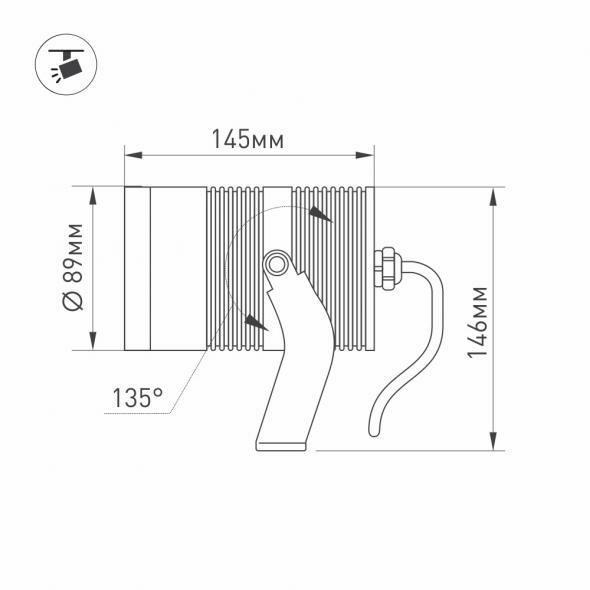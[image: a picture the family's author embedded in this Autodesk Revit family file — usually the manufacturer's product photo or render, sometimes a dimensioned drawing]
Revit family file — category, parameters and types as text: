
# Revit family: RAY-R89
name_source: partatom
category: Осветительные приборы
revit_build: Autodesk Revit 2017 (Build: 20160225_1515(x64)
units: mm (PartAtom-declared; Revit-internal decimal feet)

## family parameters
Всегда вертикально = Да
Источник света = Да
На основе рабочей плоскости = Нет
Общий = Нет
При загрузке вырезать с полостями = Нет
Размер круглого соединителя = Использовать диаметр
Тип детали = Нормальный
Точка расчета площади = Нет

## types (3) — shared parameters
ADSK_Единица измерения = шт.
ADSK_Завод-изготовитель = ARLIGHT
ADSK_Классификация нагрузок = Освещение
ADSK_Количество фаз = 1
ADSK_Количество фаз числовое = 1
ADSK_Коэффициент мощности = 0.96
ADSK_Масса_Текст = 1.37
ADSK_Наименование = Светильник
ADSK_Напряжение = 230 В
ADSK_Номинальная мощность = 25 Вт
ADSK_Полная мощность = 26 В·А
ADSK_Размер_Высота = 146 мм
ADSK_Размер_Диаметр = 89 мм
ADSK_Размер_Длина = 145 мм
ADSK_Ток = 0 А
ARL_Драйвер = Встроенный
ARL_Индекс цветопередачи = >80
ARL_Класс защиты от поражения электрическим током = I
ARL_Класс пылевлагозащиты = IP67
ARL_Материал корпуса = Металл, темно-серый
ARL_Область использования = Для ландшафтного освещения парковых и садовых дорожек, придомовых территорий, а также декоративной подсветки фасадов
ARL_Обозначение корпуса = Корпус круглый, алюминий, цвет темно-серый
ARL_Серия = RAY
ARL_Способ монтажа = Кронштейн
ARL_Тип товара = Светильник
ARL_Угол обзора = 24°
ARL_Цвет покрытия = Темно-серый
URL = https://arlight.ru
Видимая форма излучения при визуализации = Нет
Группа модели = Светильники
Изготовитель = ARLIGHT
Изготовитель (сайт) = www.arlight.ru
Изготовитель (телефон) = 8 800 505 26 29
Излучение по диаметру окружности = 67.55 мм
Полная установленная мощность = 26 В·А
Разработчик = НТЦ Конструктор
Разработчик (URL) = https://constructor.ru
Разработчик (телефон) = +7 (495) 781-05-35
Светофильтр = 16777215
Смещение цветовой температуры при затухании лампы = <Нет>
Угол наклона = 90.00°

## per-type parameters (varying)
| type | ADSK_Код изделия | ADSK_Марка | ARL_Рабочая температура окружающей среды | ARL_Цвет свечения | Комментарии к типоразмеру | Описание | Файл фотометрической сетки |
| 029699 Светильник ALT-RAY-R89-25W Day4000 (DG, 24 deg, 230V) | Арт. 029699 | ALT-RAY-R89-25W Day4000 | -40...+60 °C | Дневной 4000K | Арт. 029699 | Уличный светодиодный светильник, мощность 25 Вт, угол освещения 24°. Цвет ДНЕВНОЙ 4000К, световой поток 2100лм. Влагозащищенный корпус IP67 - темно-серый алюминий, экран из закаленного стекла. Угол поворота корпуса в вертикальной плоскости 135°. Питание 230 В, мощность 25 Вт. Размеры DxH - Ø89x145 мм. В комплекте 1 м провод | 029699 ALT-RAY-R89-25W Day4000 (DG, 24 deg, 230V).ies |
| 026448 Светильник ALT-RAY-R89-25W Warm3000 (DG, 24 deg, 230V) | Арт. 026448 | ALT-RAY-R89-25W Warm3000 | -40...+60 °C | Теплый 3000K | Арт. 026448 | Уличный светодиодный светильник, мощность 25 Вт, угол освещения 24°. Цвет ТЕПЛЫЙ 3000К, световой поток 1965лм. Влагозащищенный корпус IP67 - темно-серый алюминий, экран из закаленного стекла. Угол поворота корпуса в вертикальной плоскости 135°. Питание 230 В, мощность 25 Вт. Размеры DxH - Ø89x145 мм. В комплекте 1 м провод | 026448 ALT-RAY-R89-25W Warm3000 (DG, 24 deg, 230V).ies |
| 030342 Светильник ALT-RAY-R89-25W White6000 (DG, 24 deg, 230V) | Арт. 030342 | ALT-RAY-R89-25W White6000 | -40…+60 | Белый 6000K | Арт. 030342 | Уличный светодиодный светильник, мощность 25Вт, угол освещения 24°. Цвет ДНЕВНОЙ 4000К, световой поток 2100лм. Влагозащищенный корпус IP67 - темно-серый алюминий, экран из закаленного стекла. Угол поворота корпуса в вертикальной плоскости 135°. Питание 230В, мощность 25 Вт. Размеры DxH - Ø89x145мм. В комплекте 1м провод | 030342 ALT-RAY-R89-25W White6000 (DG, 24 deg, 230V).ies |
